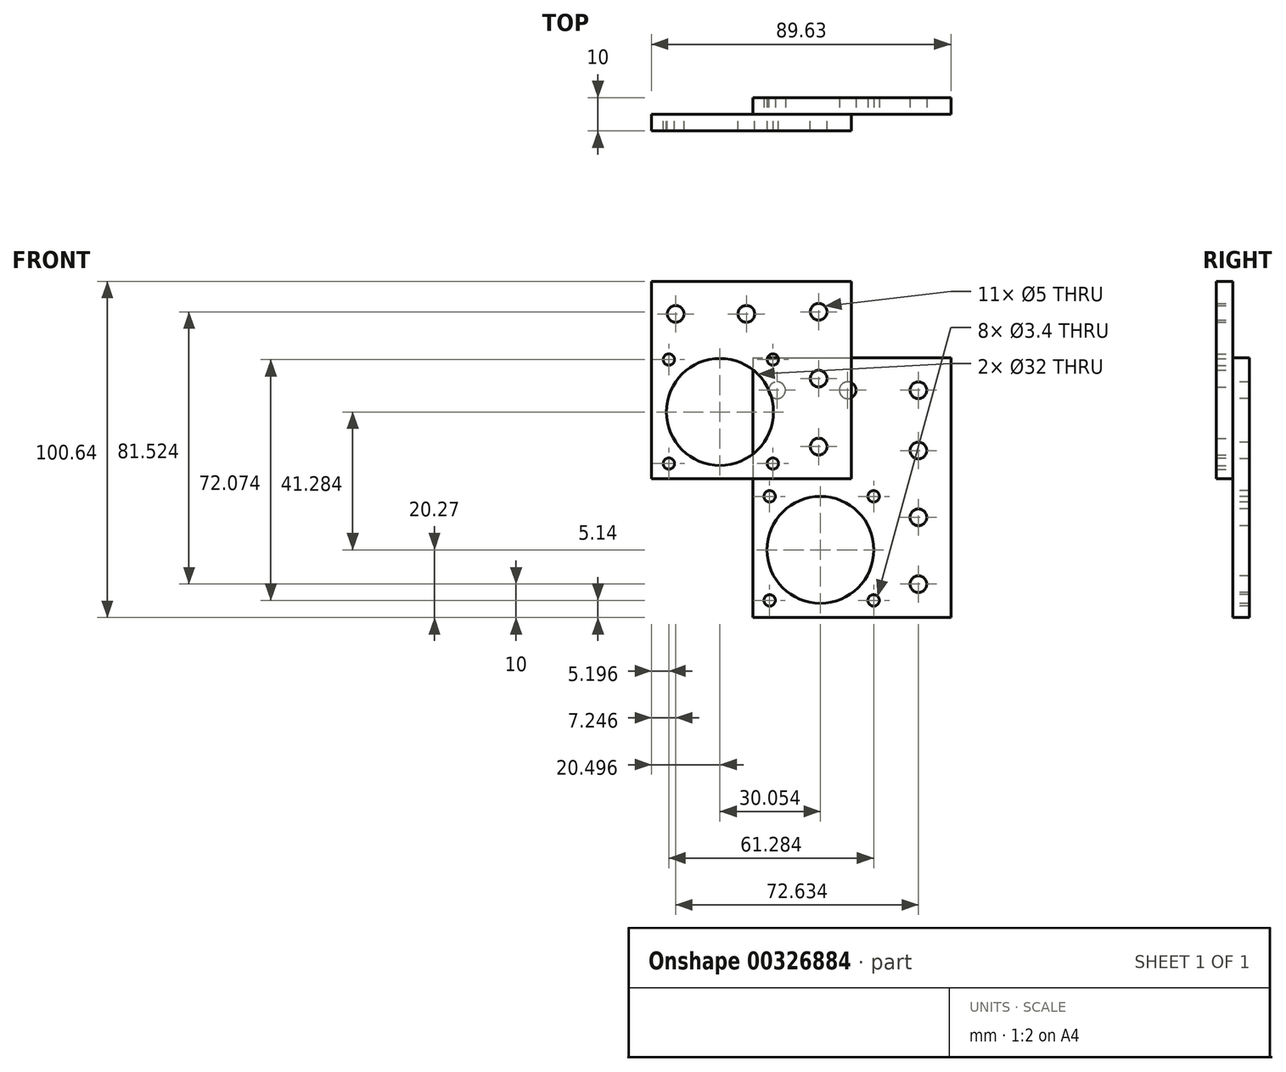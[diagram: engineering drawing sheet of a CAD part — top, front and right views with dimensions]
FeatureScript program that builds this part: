
annotation { "Feature Type Name" : "Feature", "Feature Type Description" : "" }
export const myFeature = defineFeature(function(context is Context, id is Id, definition is map)
    precondition{}
    {
        {
            var Q0;
            Q0=qCreatedBy(makeId("Front.planeOp"),FACE);
            var sketch = newSketch(context, id + "F0", { "sketchPlane" : qUnion([Q0])});
            skLineSegment(sketch, "E0.bottom", {"start": v(0, 0) * mm, "end": v(59.3, 0) * mm});
            skLineSegment(sketch, "E0.top", {"start": v(0, -77.8) * mm, "end": v(59.3, -77.8) * mm});
            skLineSegment(sketch, "E0.left", {"start": v(0, 0) * mm, "end": v(0, -77.8) * mm});
            skLineSegment(sketch, "E0.right", {"start": v(59.3, 0) * mm, "end": v(59.3, -77.8) * mm});
            skCircle(sketch, "E1", {"center": v(7.25, -9.75) * mm, "radius": 2.5 * mm});
            skCircle(sketch, "E2", {"center": v(20.22, -57.53) * mm, "radius": 16 * mm});
            skCircle(sketch, "E3", {"center": v(36.15, -41.53) * mm, "radius": 1.7 * mm});
            skCircle(sketch, "E4", {"center": v(36.15, -72.66) * mm, "radius": 1.7 * mm});
            skCircle(sketch, "E5", {"center": v(5.02, -72.66) * mm, "radius": 1.7 * mm});
            skCircle(sketch, "E6", {"center": v(5.02, -41.53) * mm, "radius": 1.7 * mm});
            skCircle(sketch, "E7", {"center": v(28.4, -9.75) * mm, "radius": 2.5 * mm});
            skCircle(sketch, "E8", {"center": v(49.55, -9.75) * mm, "radius": 2.5 * mm});
            skCircle(sketch, "E9", {"center": v(49.55, -27.8) * mm, "radius": 2.5 * mm});
            skCircle(sketch, "E10", {"center": v(49.55, -47.8) * mm, "radius": 2.5 * mm});
            skCircle(sketch, "E11", {"center": v(49.55, -67.8) * mm, "radius": 2.5 * mm});
            skSolve(sketch);
        }
        {
            var Q0;
            Q0=makeQuery(id+"F0.imprint","IMPRINT",FACE,{"disambiguationData":[TD([[makeQuery(id+"F0.imprint","IMPRINT",EDGE,{"derivedFrom":sQuery(id+"F0.wireOp",EDGE,"E0.bottom")}),-1.0]])]});
            extrude(context, id + "F1", {"entities" : qUnion([Q0]), "oppositeDirection" : true, "depth" : 5 * mm});
        }
        {
            var Q0;
            Q0=qCreatedBy(makeId("Front.planeOp"),FACE);
            var sketch = newSketch(context, id + "F2", { "sketchPlane" : qUnion([Q0])});
            skLineSegment(sketch, "E12.bottom", {"start": v(-30.33, 22.84) * mm, "end": v(29.45, 22.84) * mm});
            skLineSegment(sketch, "E12.top", {"start": v(-30.33, -36.28) * mm, "end": v(29.45, -36.28) * mm});
            skLineSegment(sketch, "E12.left", {"start": v(-30.33, 22.84) * mm, "end": v(-30.33, -36.28) * mm});
            skLineSegment(sketch, "E12.right", {"start": v(29.45, 22.84) * mm, "end": v(29.45, -36.28) * mm});
            skCircle(sketch, "E13", {"center": v(-23.08, 13.1) * mm, "radius": 2.5 * mm});
            skCircle(sketch, "E14", {"center": v(-9.83, -16.25) * mm, "radius": 16 * mm});
            skCircle(sketch, "E15", {"center": v(6, -0.59) * mm, "radius": 1.7 * mm});
            skCircle(sketch, "E16", {"center": v(6, -31.72) * mm, "radius": 1.7 * mm});
            skCircle(sketch, "E17", {"center": v(-25.13, -31.72) * mm, "radius": 1.7 * mm});
            skCircle(sketch, "E18", {"center": v(-25.13, -0.59) * mm, "radius": 1.7 * mm});
            skCircle(sketch, "E19", {"center": v(-1.93, 13.1) * mm, "radius": 2.5 * mm});
            skCircle(sketch, "E20", {"center": v(19.7, 13.72) * mm, "radius": 2.5 * mm});
            skCircle(sketch, "E21", {"center": v(19.7, -6.28) * mm, "radius": 2.5 * mm});
            skCircle(sketch, "E22", {"center": v(19.7, -26.64) * mm, "radius": 2.5 * mm});
            skSolve(sketch);
        }
        {
            var Q0;
            Q0=makeQuery(id+"F2.imprint","IMPRINT",FACE,{"disambiguationData":[TD([[makeQuery(id+"F2.imprint","IMPRINT",EDGE,{"derivedFrom":sQuery(id+"F2.wireOp",EDGE,"E12.bottom")}),-1.0]])]});
            extrude(context, id + "F3", {"entities" : qUnion([Q0]), "depth" : 5 * mm});
        }
    });
